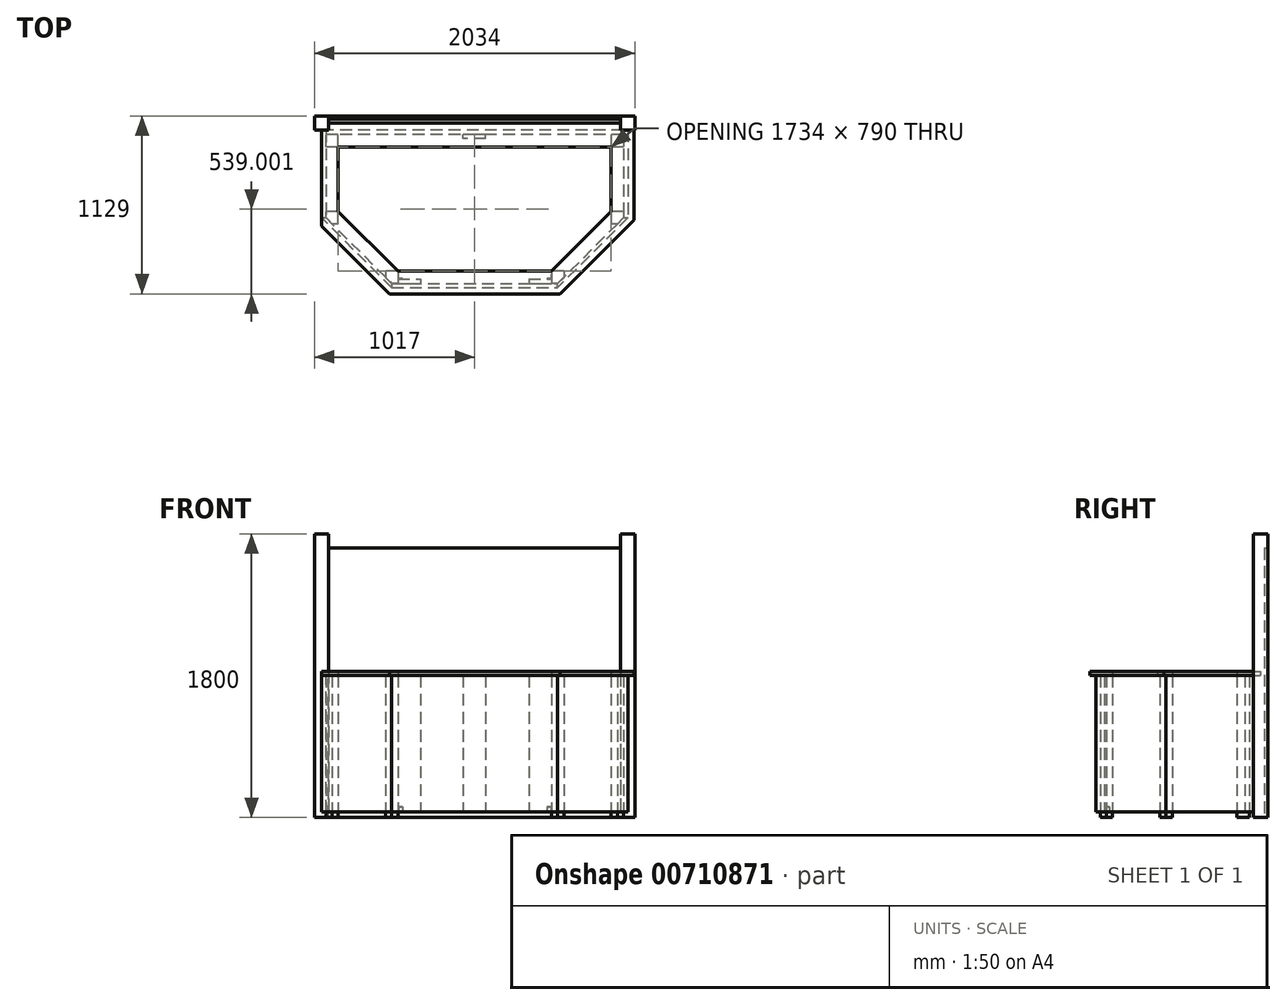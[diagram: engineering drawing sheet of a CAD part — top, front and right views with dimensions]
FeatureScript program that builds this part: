
annotation { "Feature Type Name" : "Feature", "Feature Type Description" : "" }
export const myFeature = defineFeature(function(context is Context, id is Id, definition is map)
    precondition{}
    {
        {
            var Q0;
            Q0=qCreatedBy(makeId("Top.planeOp"),FACE);
            var sketch = newSketch(context, id + "F0", { "sketchPlane" : qUnion([Q0])});
            skLineSegment(sketch, "E0.bottom", {"start": v(-243.5, 53.36) * mm, "end": v(-321.5, 53.36) * mm});
            skLineSegment(sketch, "E0.top", {"start": v(-243.5, 131.36) * mm, "end": v(-321.5, 131.36) * mm});
            skLineSegment(sketch, "E0.left", {"start": v(-243.5, 53.36) * mm, "end": v(-243.5, 131.36) * mm});
            skLineSegment(sketch, "E0.right", {"start": v(-321.5, 53.36) * mm, "end": v(-321.5, 131.36) * mm});
            skPoint(sketch, "E0.middle", {"position": v(-282.5, 92.36) * mm});
            skLineSegment(sketch, "E1.bottom", {"start": v(1568.5, 131.36) * mm, "end": v(1490.5, 131.36) * mm});
            skLineSegment(sketch, "E1.top", {"start": v(1568.5, 53.36) * mm, "end": v(1490.5, 53.36) * mm});
            skLineSegment(sketch, "E1.left", {"start": v(1568.5, 131.36) * mm, "end": v(1568.5, 53.36) * mm});
            skLineSegment(sketch, "E1.right", {"start": v(1490.5, 131.36) * mm, "end": v(1490.5, 53.36) * mm});
            skPoint(sketch, "E1.middle", {"position": v(1529.5, 92.36) * mm});
            skPoint(sketch, "E1.middle.positionSnap0", {"position": v(-243.5, 92.36) * mm});
            skPoint(sketch, "E1.centerSnap0", {"position": v(-243.5, 92.36) * mm});
            skLineSegment(sketch, "E2.bottom", {"start": v(-243.5, -435.84) * mm, "end": v(-282.5, -435.84) * mm});
            skLineSegment(sketch, "E2.top", {"start": v(-243.5, -357.84) * mm, "end": v(-321.5, -357.84) * mm});
            skLineSegment(sketch, "E2.left", {"start": v(-243.5, -435.84) * mm, "end": v(-243.5, -357.84) * mm});
            skLineSegment(sketch, "E2.right", {"start": v(-321.5, -396.84) * mm, "end": v(-321.5, -357.84) * mm});
            skPoint(sketch, "E2.middle", {"position": v(-282.5, -396.84) * mm});
            skPoint(sketch, "E2.middle.positionSnap0", {"position": v(-282.5, 53.36) * mm});
            skPoint(sketch, "E2.centerSnap0", {"position": v(-282.5, 53.36) * mm});
            skLineSegment(sketch, "E3.bottom", {"start": v(1568.5, -357.84) * mm, "end": v(1490.5, -357.84) * mm});
            skLineSegment(sketch, "E3.top", {"start": v(1529.5, -435.84) * mm, "end": v(1490.5, -435.84) * mm});
            skLineSegment(sketch, "E3.left", {"start": v(1568.5, -357.84) * mm, "end": v(1568.5, -396.84) * mm});
            skLineSegment(sketch, "E3.right", {"start": v(1490.5, -357.84) * mm, "end": v(1490.5, -435.84) * mm});
            skPoint(sketch, "E3.middle", {"position": v(1529.5, -396.84) * mm});
            skPoint(sketch, "E3.middle.positionSnap0", {"position": v(1529.5, 53.36) * mm});
            skPoint(sketch, "E3.centerSnap0", {"position": v(1529.5, 53.36) * mm});
            skLineSegment(sketch, "E4", {"start": v(1568.51, -396.82) * mm, "end": v(1529.5, -435.84) * mm});
            skLineSegment(sketch, "E5", {"start": v(-321.5, -396.84) * mm, "end": v(-282.5, -435.84) * mm});
            skLineSegment(sketch, "E6.bottom", {"start": v(135.3, -736.64) * mm, "end": v(57.3, -736.64) * mm});
            skLineSegment(sketch, "E6.top", {"start": v(135.3, -814.64) * mm, "end": v(96.3, -814.64) * mm});
            skLineSegment(sketch, "E6.left", {"start": v(135.3, -736.64) * mm, "end": v(135.3, -814.64) * mm});
            skLineSegment(sketch, "E6.right", {"start": v(57.3, -736.64) * mm, "end": v(57.3, -775.64) * mm});
            skPoint(sketch, "E6.middle", {"position": v(96.3, -775.64) * mm});
            skLineSegment(sketch, "E7.bottom", {"start": v(1189.7, -736.64) * mm, "end": v(1111.7, -736.64) * mm});
            skLineSegment(sketch, "E7.top", {"start": v(1150.7, -814.64) * mm, "end": v(1111.7, -814.64) * mm});
            skLineSegment(sketch, "E7.left", {"start": v(1189.7, -736.64) * mm, "end": v(1189.7, -775.64) * mm});
            skLineSegment(sketch, "E7.right", {"start": v(1111.7, -736.64) * mm, "end": v(1111.7, -814.64) * mm});
            skPoint(sketch, "E7.middle", {"position": v(1150.7, -775.64) * mm});
            skPoint(sketch, "E7.middle.positionSnap0", {"position": v(135.3, -775.64) * mm});
            skPoint(sketch, "E7.centerSnap0", {"position": v(135.3, -775.64) * mm});
            skLineSegment(sketch, "E8", {"start": v(1150.7, -814.64) * mm, "end": v(1189.7, -775.64) * mm});
            skLineSegment(sketch, "E9", {"start": v(57.3, -775.64) * mm, "end": v(96.3, -814.64) * mm});
            skSolve(sketch);
        }
        {
            var Q0;
            Q0 = qSketchRegion(id + "F0", true);
            extrude(context, id + "F1", {"entities" : qUnion([Q0]), "depth" : 900 * mm, "offsetDistance" : 25 * mm});
        }
        {
            var Q0;
            Q0=makeQuery(id+"F1.opExtrude","SWEPT_FACE",FACE,{"disambiguationData":[OSD([sQuery(id+"F0.wireOp",EDGE,"E1.bottom")])]});
            var sketch = newSketch(context, id + "F2", { "sketchPlane" : qUnion([Q0])});
            skLineSegment(sketch, "E10.bottom", {"start": v(-1568.5, 36) * mm, "end": v(321.5, 36) * mm});
            skLineSegment(sketch, "E10.top", {"start": v(-1568.5, 900) * mm, "end": v(321.5, 900) * mm});
            skLineSegment(sketch, "E10.left", {"start": v(-1568.5, 36) * mm, "end": v(-1568.5, 900) * mm});
            skLineSegment(sketch, "E10.right", {"start": v(321.5, 36) * mm, "end": v(321.5, 900) * mm});
            skSolve(sketch);
        }
        {
            var Q0;
            Q0 = qSketchRegion(id + "F2", true);
            extrude(context, id + "F3", {"entities" : qUnion([Q0]), "depth" : 27 * mm, "offsetDistance" : 25 * mm});
        }
        {
            var Q0;
            Q0=makeQuery(id+"F3.opExtrude","SWEPT_FACE",FACE,{"disambiguationData":[OSD([sQuery(id+"F2.wireOp",EDGE,"E10.right")])]});
            var sketch = newSketch(context, id + "F4", { "sketchPlane" : qUnion([Q0])});
            skLineSegment(sketch, "E11.bottom", {"start": v(-158.36, 36) * mm, "end": v(396.84, 36) * mm});
            skLineSegment(sketch, "E11.top", {"start": v(-158.36, 900) * mm, "end": v(396.84, 900) * mm});
            skLineSegment(sketch, "E11.left", {"start": v(-158.36, 36) * mm, "end": v(-158.36, 900) * mm});
            skLineSegment(sketch, "E11.right", {"start": v(396.84, 36) * mm, "end": v(396.84, 900) * mm});
            skSolve(sketch);
        }
        {
            var Q0;
            Q0 = qSketchRegion(id + "F4", true);
            extrude(context, id + "F5", {"entities" : qUnion([Q0]), "depth" : 27 * mm, "offsetDistance" : 25 * mm});
        }
        {
            var Q0;
            Q0=makeQuery(id+"F3.opExtrude","SWEPT_FACE",FACE,{"disambiguationData":[OSD([sQuery(id+"F2.wireOp",EDGE,"E10.left")])]});
            var sketch = newSketch(context, id + "F6", { "sketchPlane" : qUnion([Q0])});
            skLineSegment(sketch, "E12.bottom", {"start": v(158.36, 36) * mm, "end": v(-396.84, 36) * mm});
            skLineSegment(sketch, "E12.top", {"start": v(158.36, 900) * mm, "end": v(-396.84, 900) * mm});
            skLineSegment(sketch, "E12.left", {"start": v(158.36, 36) * mm, "end": v(158.36, 900) * mm});
            skLineSegment(sketch, "E12.right", {"start": v(-396.84, 36) * mm, "end": v(-396.84, 900) * mm});
            skSolve(sketch);
        }
        {
            var Q0;
            Q0 = qSketchRegion(id + "F6", true);
            extrude(context, id + "F7", {"entities" : qUnion([Q0]), "depth" : 27 * mm, "offsetDistance" : 25 * mm});
        }
        {
            var Q0;
            Q0=makeQuery(id+"F1.opExtrude","SWEPT_FACE",FACE,{"disambiguationData":[OSD([sQuery(id+"F0.wireOp",EDGE,"E6.top")])]});
            var sketch = newSketch(context, id + "F8", { "sketchPlane" : qUnion([Q0])});
            skLineSegment(sketch, "E13.bottom", {"start": v(96.3, 900) * mm, "end": v(1150.7, 900) * mm});
            skLineSegment(sketch, "E13.top", {"start": v(96.3, 36) * mm, "end": v(1150.7, 36) * mm});
            skLineSegment(sketch, "E13.left", {"start": v(96.3, 900) * mm, "end": v(96.3, 36) * mm});
            skLineSegment(sketch, "E13.right", {"start": v(1150.7, 900) * mm, "end": v(1150.7, 36) * mm});
            skSolve(sketch);
        }
        {
            var Q0;
            Q0 = qSketchRegion(id + "F8", true);
            extrude(context, id + "F9", {"entities" : qUnion([Q0]), "depth" : 27 * mm, "offsetDistance" : 25 * mm});
        }
        {
            var Q0;
            Q0=makeQuery(id+"F1.opExtrude","CAP_FACE",FACE,{"disambiguationData":[OSD([sQuery(id+"F0.wireOp",EDGE,"E7.bottom"),sQuery(id+"F0.wireOp",EDGE,"E7.top"),sQuery(id+"F0.wireOp",EDGE,"E7.left"),sQuery(id+"F0.wireOp",EDGE,"E7.right"),sQuery(id+"F0.wireOp",EDGE,"E8")])],"isStart":false});
            var sketch = newSketch(context, id + "F10", { "sketchPlane" : qUnion([Q0])});
            skLineSegment(sketch, "E14", {"start": v(1150.7, -814.64) * mm, "end": v(1568.5, -396.84) * mm});
            skLineSegment(sketch, "E15", {"start": v(1568.5, -396.84) * mm, "end": v(1595.5, -396.84) * mm});
            skLineSegment(sketch, "E16", {"start": v(1595.5, -396.84) * mm, "end": v(1150.7, -841.64) * mm});
            skLineSegment(sketch, "E17", {"start": v(1150.7, -841.64) * mm, "end": v(1150.7, -814.64) * mm});
            skSolve(sketch);
        }
        {
            var Q0;
            Q0 = qSketchRegion(id + "F10", true);
            extrude(context, id + "F11", {"entities" : qUnion([Q0]), "oppositeDirection" : true, "depth" : 864 * mm, "offsetDistance" : 25 * mm});
        }
        {
            var Q0;
            Q0=makeQuery(id+"F1.opExtrude","CAP_FACE",FACE,{"disambiguationData":[OSD([sQuery(id+"F0.wireOp",EDGE,"E2.bottom"),sQuery(id+"F0.wireOp",EDGE,"E2.top"),sQuery(id+"F0.wireOp",EDGE,"E2.left"),sQuery(id+"F0.wireOp",EDGE,"E2.right"),sQuery(id+"F0.wireOp",EDGE,"E5")])],"isStart":false});
            var sketch = newSketch(context, id + "F12", { "sketchPlane" : qUnion([Q0])});
            skLineSegment(sketch, "E18", {"start": v(-321.5, -396.84) * mm, "end": v(96.3, -814.64) * mm});
            skLineSegment(sketch, "E19", {"start": v(96.3, -814.64) * mm, "end": v(96.3, -841.64) * mm});
            skLineSegment(sketch, "E20", {"start": v(96.3, -841.64) * mm, "end": v(-348.5, -396.84) * mm});
            skLineSegment(sketch, "E21", {"start": v(-348.5, -396.84) * mm, "end": v(-321.5, -396.84) * mm});
            skSolve(sketch);
        }
        {
            var Q0;
            Q0 = qSketchRegion(id + "F12", true);
            extrude(context, id + "F13", {"entities" : qUnion([Q0]), "oppositeDirection" : true, "depth" : 864 * mm, "offsetDistance" : 25 * mm});
        }
        {
            var Q0;
            Q0=makeQuery(id+"F7.opExtrude","SWEPT_FACE",FACE,{"disambiguationData":[OSD([sQuery(id+"F6.wireOp",EDGE,"E12.top")])]});
            var sketch = newSketch(context, id + "F14", { "sketchPlane" : qUnion([Q0])});
            skLineSegment(sketch, "E22", {"start": v(1490.5, 53.36) * mm, "end": v(1595.5, 158.36) * mm});
            skLineSegment(sketch, "E23", {"start": v(1634.5, 158.36) * mm, "end": v(1634.5, -411.32) * mm});
            skLineSegment(sketch, "E24", {"start": v(1634.5, -411.32) * mm, "end": v(1490.5, -357.84) * mm});
            skLineSegment(sketch, "E25", {"start": v(1490.5, -357.84) * mm, "end": v(1490.5, 53.36) * mm});
            skLineSegment(sketch, "E26", {"start": v(1490.5, -357.84) * mm, "end": v(1111.7, -736.64) * mm});
            skLineSegment(sketch, "E27", {"start": v(1165.18, -880.64) * mm, "end": v(1111.7, -736.64) * mm});
            skLineSegment(sketch, "E28", {"start": v(1165.18, -880.64) * mm, "end": v(1634.5, -411.32) * mm});
            skLineSegment(sketch, "E29", {"start": v(135.3, -736.64) * mm, "end": v(81.81, -880.64) * mm});
            skLineSegment(sketch, "E30", {"start": v(81.81, -880.64) * mm, "end": v(1165.18, -880.64) * mm});
            skLineSegment(sketch, "E31", {"start": v(135.3, -736.64) * mm, "end": v(1111.7, -736.64) * mm});
            skLineSegment(sketch, "E32", {"start": v(135.3, -736.64) * mm, "end": v(-243.5, -357.84) * mm});
            skLineSegment(sketch, "E33", {"start": v(-243.5, -357.84) * mm, "end": v(-348.5, -396.84) * mm});
            skLineSegment(sketch, "E34", {"start": v(-348.5, -450.32) * mm, "end": v(81.81, -880.64) * mm});
            skLineSegment(sketch, "E35", {"start": v(-243.5, -357.84) * mm, "end": v(-243.5, 53.36) * mm});
            skLineSegment(sketch, "E36", {"start": v(-348.5, 158.36) * mm, "end": v(-243.5, 53.36) * mm});
            skLineSegment(sketch, "E37", {"start": v(-243.5, 53.36) * mm, "end": v(1490.5, 53.36) * mm});
            skLineSegment(sketch, "E38", {"start": v(-348.5, 158.36) * mm, "end": v(1595.5, 158.36) * mm});
            skLineSegment(sketch, "E39", {"start": v(1595.5, 158.36) * mm, "end": v(1634.5, 158.36) * mm});
            skLineSegment(sketch, "E40", {"start": v(-348.5, 158.36) * mm, "end": v(-348.5, -396.84) * mm});
            skLineSegment(sketch, "E41", {"start": v(-348.5, -396.84) * mm, "end": v(-348.5, -450.32) * mm});
            skLineSegment(sketch, "E42", {"start": v(-348.5, 158.36) * mm, "end": v(-303.5, 158.36) * mm});
            skLineSegment(sketch, "E43", {"start": v(-303.5, 158.36) * mm, "end": v(-303.5, 203.36) * mm});
            skLineSegment(sketch, "E44", {"start": v(-303.5, 203.36) * mm, "end": v(1550.5, 203.36) * mm});
            skLineSegment(sketch, "E45", {"start": v(1550.5, 203.36) * mm, "end": v(1550.5, 158.36) * mm});
            skSolve(sketch);
        }
        {
            var Q0;
            Q0 = qSketchRegion(id + "F14", true);
            extrude(context, id + "F15", {"entities" : qUnion([Q0]), "depth" : 27 * mm, "offsetDistance" : 25 * mm});
        }
        {
            var Q0;
            Q0=qCreatedBy(makeId("Top.planeOp"),FACE);
            var sketch = newSketch(context, id + "F16", { "sketchPlane" : qUnion([Q0])});
            skLineSegment(sketch, "E46.bottom", {"start": v(1550.5, 158.36) * mm, "end": v(1640.5, 158.36) * mm});
            skLineSegment(sketch, "E46.top", {"start": v(1550.5, 248.36) * mm, "end": v(1640.5, 248.36) * mm});
            skLineSegment(sketch, "E46.left", {"start": v(1550.5, 158.36) * mm, "end": v(1550.5, 248.36) * mm});
            skLineSegment(sketch, "E46.right", {"start": v(1640.5, 158.36) * mm, "end": v(1640.5, 248.36) * mm});
            skLineSegment(sketch, "E47.bottom", {"start": v(-393.5, 158.36) * mm, "end": v(-303.5, 158.36) * mm});
            skLineSegment(sketch, "E47.top", {"start": v(-393.5, 248.36) * mm, "end": v(-303.5, 248.36) * mm});
            skLineSegment(sketch, "E47.left", {"start": v(-393.5, 158.36) * mm, "end": v(-393.5, 248.36) * mm});
            skLineSegment(sketch, "E47.right", {"start": v(-303.5, 158.36) * mm, "end": v(-303.5, 248.36) * mm});
            skSolve(sketch);
        }
        {
            var Q0;
            Q0 = qSketchRegion(id + "F16", true);
            extrude(context, id + "F17", {"entities" : qUnion([Q0]), "depth" : 1800 * mm, "offsetDistance" : 25 * mm});
        }
        {
            var Q0;
            Q0=makeQuery(id+"F17.opExtrude","SWEPT_FACE",FACE,{"disambiguationData":[OSD([sQuery(id+"F16.wireOp",EDGE,"E46.top")])]});
            var sketch = newSketch(context, id + "F18", { "sketchPlane" : qUnion([Q0])});
            skLineSegment(sketch, "E48.bottom", {"start": v(-1550.5, 0) * mm, "end": v(303.5, 0) * mm});
            skLineSegment(sketch, "E48.top", {"start": v(-1550.5, 1711.13) * mm, "end": v(303.5, 1711.13) * mm});
            skLineSegment(sketch, "E48.left", {"start": v(-1550.5, 0) * mm, "end": v(-1550.5, 1711.13) * mm});
            skLineSegment(sketch, "E48.right", {"start": v(303.5, 0) * mm, "end": v(303.5, 1711.13) * mm});
            skSolve(sketch);
        }
        {
            var Q0;
            Q0 = qSketchRegion(id + "F18", true);
            extrude(context, id + "F19", {"entities" : qUnion([Q0]), "oppositeDirection" : true, "depth" : 20 * mm, "offsetDistance" : 25 * mm});
        }
        {
            var Q0;
            Q0=makeQuery(id+"F9.opExtrude","CAP_FACE",FACE,{"disambiguationData":[OSD([sQuery(id+"F8.wireOp",EDGE,"E13.bottom"),sQuery(id+"F8.wireOp",EDGE,"E13.top"),sQuery(id+"F8.wireOp",EDGE,"E13.left"),sQuery(id+"F8.wireOp",EDGE,"E13.right")])],"isStart":true});
            var sketch = newSketch(context, id + "F20", { "sketchPlane" : qUnion([Q0])});
            skLineSegment(sketch, "E49.bottom", {"start": v(-1111.7, 900) * mm, "end": v(-967.7, 900) * mm});
            skLineSegment(sketch, "E49.top", {"start": v(-1111.7, 36) * mm, "end": v(-967.7, 36) * mm});
            skLineSegment(sketch, "E49.left", {"start": v(-1111.7, 900) * mm, "end": v(-1111.7, 36) * mm});
            skLineSegment(sketch, "E49.right", {"start": v(-967.7, 900) * mm, "end": v(-967.7, 36) * mm});
            skLineSegment(sketch, "E50.bottom", {"start": v(-135.3, 900) * mm, "end": v(-279.3, 900) * mm});
            skLineSegment(sketch, "E50.top", {"start": v(-135.3, 36) * mm, "end": v(-279.3, 36) * mm});
            skLineSegment(sketch, "E50.left", {"start": v(-135.3, 900) * mm, "end": v(-135.3, 36) * mm});
            skLineSegment(sketch, "E50.right", {"start": v(-279.3, 900) * mm, "end": v(-279.3, 36) * mm});
            skSolve(sketch);
        }
        {
            var Q0;
            Q0 = qSketchRegion(id + "F20", true);
            extrude(context, id + "F21", {"entities" : qUnion([Q0]), "depth" : 27 * mm, "offsetDistance" : 25 * mm});
        }
        {
            var Q0;
            Q0=makeQuery(id+"F21.opExtrude","SWEPT_FACE",FACE,{"disambiguationData":[OSD([sQuery(id+"F20.wireOp",EDGE,"E50.top")])]});
            var sketch = newSketch(context, id + "F22", { "sketchPlane" : qUnion([Q0])});
            skLineSegment(sketch, "E51", {"start": v(165.3, 787.64) * mm, "end": v(165.3, 782.64) * mm});
            skLineSegment(sketch, "E52", {"start": v(165.3, 782.64) * mm, "end": v(140.3, 782.64) * mm});
            skLineSegment(sketch, "E53", {"start": v(140.3, 782.64) * mm, "end": v(140.3, 757.64) * mm});
            skLineSegment(sketch, "E54", {"start": v(140.3, 757.64) * mm, "end": v(135.3, 757.64) * mm});
            skLineSegment(sketch, "E55", {"start": v(135.3, 757.64) * mm, "end": v(135.3, 787.64) * mm});
            skLineSegment(sketch, "E56", {"start": v(135.3, 787.64) * mm, "end": v(165.3, 787.64) * mm});
            skLineSegment(sketch, "E57", {"start": v(1081.7, 787.64) * mm, "end": v(1111.7, 787.64) * mm});
            skLineSegment(sketch, "E58", {"start": v(1111.7, 787.64) * mm, "end": v(1111.7, 757.64) * mm});
            skLineSegment(sketch, "E59", {"start": v(1111.7, 757.64) * mm, "end": v(1106.7, 757.64) * mm});
            skLineSegment(sketch, "E60", {"start": v(1106.7, 757.64) * mm, "end": v(1106.7, 782.64) * mm});
            skLineSegment(sketch, "E61", {"start": v(1106.7, 782.64) * mm, "end": v(1081.7, 782.64) * mm});
            skLineSegment(sketch, "E62", {"start": v(1081.7, 782.64) * mm, "end": v(1081.7, 787.64) * mm});
            skSolve(sketch);
        }
        {
            var Q0;
            Q0 = qSketchRegion(id + "F22", true);
            extrude(context, id + "F23", {"entities" : qUnion([Q0]), "oppositeDirection" : true, "depth" : 30 * mm, "offsetDistance" : 25 * mm});
        }
        {
            var Q0;
            Q0=makeQuery(id+"F3.opExtrude","CAP_FACE",FACE,{"disambiguationData":[OSD([sQuery(id+"F2.wireOp",EDGE,"E10.bottom"),sQuery(id+"F2.wireOp",EDGE,"E10.top"),sQuery(id+"F2.wireOp",EDGE,"E10.left"),sQuery(id+"F2.wireOp",EDGE,"E10.right")])],"isStart":true});
            var sketch = newSketch(context, id + "F24", { "sketchPlane" : qUnion([Q0])});
            skLineSegment(sketch, "E63.bottom", {"start": v(549, 900) * mm, "end": v(693, 900) * mm});
            skLineSegment(sketch, "E63.top", {"start": v(549, 36) * mm, "end": v(693, 36) * mm});
            skLineSegment(sketch, "E63.left", {"start": v(549, 900) * mm, "end": v(549, 36) * mm});
            skLineSegment(sketch, "E63.right", {"start": v(693, 900) * mm, "end": v(693, 36) * mm});
            skSolve(sketch);
        }
        {
            var Q0;
            Q0 = qSketchRegion(id + "F24", true);
            extrude(context, id + "F25", {"entities" : qUnion([Q0]), "depth" : 27 * mm, "offsetDistance" : 25 * mm});
        }
    });
